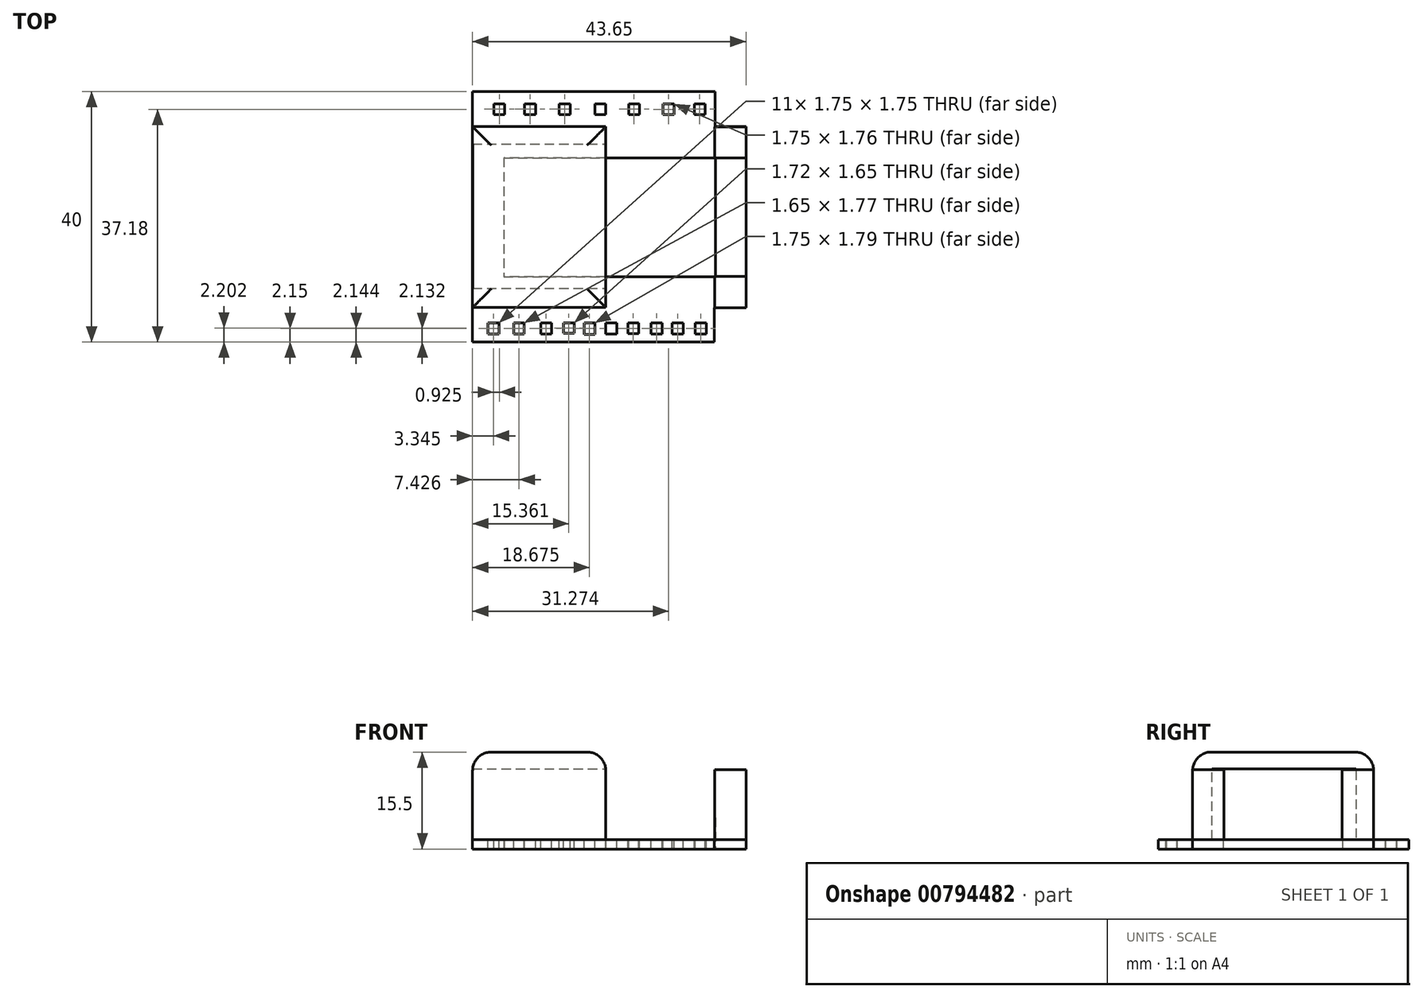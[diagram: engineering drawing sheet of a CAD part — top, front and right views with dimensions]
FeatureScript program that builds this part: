
annotation { "Feature Type Name" : "Feature", "Feature Type Description" : "" }
export const myFeature = defineFeature(function(context is Context, id is Id, definition is map)
    precondition{}
    {
        {
            var Q0;
            Q0=qCreatedBy(makeId("Top.planeOp"),FACE);
            var sketch = newSketch(context, id + "F0", { "sketchPlane" : qUnion([Q0])});
            skLineSegment(sketch, "E0.bottom", {"start": v(-21.27, 7.67) * mm, "end": v(22.37, 7.67) * mm});
            skLineSegment(sketch, "E0.top", {"start": v(-21.27, -21.23) * mm, "end": v(22.37, -21.23) * mm});
            skLineSegment(sketch, "E0.left", {"start": v(-21.27, 7.67) * mm, "end": v(-21.27, -21.23) * mm});
            skLineSegment(sketch, "E0.right", {"start": v(22.37, 7.67) * mm, "end": v(22.37, -21.23) * mm});
            skLineSegment(sketch, "E1.bottom", {"start": v(22.37, 7.67) * mm, "end": v(0, 7.67) * mm});
            skLineSegment(sketch, "E1.top", {"start": v(22.37, -21.23) * mm, "end": v(0, -21.23) * mm});
            skLineSegment(sketch, "E2.bottom", {"start": v(-21.27, 7.67) * mm, "end": v(-16.27, 7.67) * mm});
            skLineSegment(sketch, "E2.top", {"start": v(-21.27, 2.67) * mm, "end": v(-16.27, 2.67) * mm});
            skLineSegment(sketch, "E2.left", {"start": v(-21.27, 7.67) * mm, "end": v(-21.27, 2.67) * mm});
            skLineSegment(sketch, "E2.right", {"start": v(-16.27, 7.67) * mm, "end": v(-16.27, 2.67) * mm});
            skLineSegment(sketch, "E3.bottom", {"start": v(-21.27, -21.23) * mm, "end": v(-16.27, -21.23) * mm});
            skLineSegment(sketch, "E3.top", {"start": v(-21.27, -16.23) * mm, "end": v(-16.27, -16.23) * mm});
            skLineSegment(sketch, "E3.left", {"start": v(-21.27, -21.23) * mm, "end": v(-21.27, -16.23) * mm});
            skLineSegment(sketch, "E3.right", {"start": v(-16.27, -21.23) * mm, "end": v(-16.27, -16.23) * mm});
            skLineSegment(sketch, "E4.bottom", {"start": v(22.37, -21.23) * mm, "end": v(17.37, -21.23) * mm});
            skLineSegment(sketch, "E4.top", {"start": v(22.37, -16.23) * mm, "end": v(17.37, -16.23) * mm});
            skLineSegment(sketch, "E4.left", {"start": v(22.37, -21.23) * mm, "end": v(22.37, -16.23) * mm});
            skLineSegment(sketch, "E4.right", {"start": v(17.37, -21.23) * mm, "end": v(17.37, -16.23) * mm});
            skLineSegment(sketch, "E5.bottom", {"start": v(22.37, 7.67) * mm, "end": v(17.37, 7.67) * mm});
            skLineSegment(sketch, "E5.top", {"start": v(22.37, 2.67) * mm, "end": v(17.37, 2.67) * mm});
            skLineSegment(sketch, "E5.left", {"start": v(22.37, 7.67) * mm, "end": v(22.37, 2.67) * mm});
            skLineSegment(sketch, "E5.right", {"start": v(17.37, 7.67) * mm, "end": v(17.37, 2.67) * mm});
            skSolve(sketch);
        }
        {
            var Q0;
            Q0 = qSketchRegion(id + "F0", true);
            extrude(context, id + "F1", {"entities" : qUnion([Q0]), "oppositeDirection" : true, "depth" : 1.5 * mm, "offsetDistance" : 25 * mm});
        }
        {
            var Q0;
            Q0=makeQuery(id+"F0.imprint","IMPRINT",FACE,{"disambiguationData":[TD([[makeQuery(id+"F0.imprint","IMPRINT",EDGE,{"derivedFrom":sQuery(id+"F0.wireOp",EDGE,"E0.bottom")}),-1.0]])]});
            var sketch = newSketch(context, id + "F2", { "sketchPlane" : qUnion([Q0])});
            skLineSegment(sketch, "E6.bottom", {"start": v(17.38, 7.65) * mm, "end": v(22.38, 7.65) * mm});
            skLineSegment(sketch, "E6.top", {"start": v(17.38, 2.65) * mm, "end": v(22.38, 2.65) * mm});
            skLineSegment(sketch, "E6.left", {"start": v(17.38, 7.65) * mm, "end": v(17.38, 2.65) * mm});
            skLineSegment(sketch, "E6.right", {"start": v(22.38, 7.65) * mm, "end": v(22.38, 2.65) * mm});
            skLineSegment(sketch, "E7.bottom", {"start": v(22.38, -21.25) * mm, "end": v(17.38, -21.25) * mm});
            skLineSegment(sketch, "E7.top", {"start": v(22.38, -16.25) * mm, "end": v(17.38, -16.25) * mm});
            skLineSegment(sketch, "E7.left", {"start": v(22.38, -21.25) * mm, "end": v(22.38, -16.25) * mm});
            skLineSegment(sketch, "E7.right", {"start": v(17.38, -21.25) * mm, "end": v(17.38, -16.25) * mm});
            skSolve(sketch);
        }
        {
            var Q0;
            Q0 = qSketchRegion(id + "F2", true);
            extrude(context, id + "F3", {"entities" : qUnion([Q0]), "operationType" : NewBodyOperationType.ADD, "depth" : 11.2 * mm, "offsetDistance" : 25 * mm});
        }
        {
            var Q0;
            Q0=makeQuery(id+"F0.imprint","IMPRINT",FACE,{"disambiguationData":[TD([[makeQuery(id+"F0.imprint","IMPRINT",EDGE,{"derivedFrom":sQuery(id+"F0.wireOp",EDGE,"E0.bottom")}),-1.0]])]});
            var sketch = newSketch(context, id + "F4", { "sketchPlane" : qUnion([Q0])});
            skLineSegment(sketch, "E8.bottom", {"start": v(-21.27, 7.67) * mm, "end": v(0, 7.67) * mm});
            skLineSegment(sketch, "E8.top", {"start": v(-21.27, -21.23) * mm, "end": v(0, -21.23) * mm});
            skLineSegment(sketch, "E8.left", {"start": v(-21.27, 7.67) * mm, "end": v(-21.27, -21.23) * mm});
            skLineSegment(sketch, "E8.right", {"start": v(0, 7.67) * mm, "end": v(0, -21.23) * mm});
            skSolve(sketch);
        }
        {
            var Q0;
            Q0 = qSketchRegion(id + "F4", true);
            extrude(context, id + "F5", {"entities" : qUnion([Q0]), "operationType" : NewBodyOperationType.ADD, "depth" : 14 * mm, "offsetDistance" : 25 * mm});
        }
        {
            var Q0;
            Q0=makeQuery(id+"F5.opExtrude","SWEPT_FACE",FACE,{"disambiguationData":[OSD([sQuery(id+"F4.wireOp",EDGE,"E8.right")])]});
            var sketch = newSketch(context, id + "F6", { "sketchPlane" : qUnion([Q0])});
            skLineSegment(sketch, "E9.bottom", {"start": v(-18.14, 11.3) * mm, "end": v(4.86, 11.3) * mm});
            skLineSegment(sketch, "E9.top", {"start": v(-18.14, 0) * mm, "end": v(4.86, 0) * mm});
            skLineSegment(sketch, "E9.left", {"start": v(-18.14, 11.3) * mm, "end": v(-18.14, 0) * mm});
            skLineSegment(sketch, "E9.right", {"start": v(4.86, 11.3) * mm, "end": v(4.86, 0) * mm});
            skLineSegment(sketch, "E10", {"start": v(4.86, 11.3) * mm, "end": v(7.67, 11.3) * mm});
            skSolve(sketch);
        }
        {
            var Q0;
            Q0 = qSketchRegion(id + "F6", true);
            extrude(context, id + "F7", {"entities" : qUnion([Q0]), "operationType" : NewBodyOperationType.REMOVE, "oppositeDirection" : true, "depth" : 37.2 * mm, "offsetDistance" : 25 * mm});
        }
        {
            var Q0;
            Q0=makeQuery(id+"F1.opExtrude","SWEPT_FACE",FACE,{"disambiguationData":[OSD([sQuery(id+"F0.wireOp",EDGE,"E0.top"),sQuery(id+"F0.wireOp",EDGE,"E1.top"),sQuery(id+"F0.wireOp",EDGE,"E3.bottom"),sQuery(id+"F0.wireOp",EDGE,"E4.bottom")])]});
            var sketch = newSketch(context, id + "F8", { "sketchPlane" : qUnion([Q0])});
            skLineSegment(sketch, "E11.bottom", {"start": v(-21.27, 0) * mm, "end": v(22.37, 0) * mm});
            skLineSegment(sketch, "E11.top", {"start": v(-21.27, -1.5) * mm, "end": v(22.37, -1.5) * mm});
            skLineSegment(sketch, "E11.left", {"start": v(-21.27, 0) * mm, "end": v(-21.27, -1.5) * mm});
            skLineSegment(sketch, "E11.right", {"start": v(22.37, 0) * mm, "end": v(22.37, -1.5) * mm});
            skSolve(sketch);
        }
        {
            var Q0;
            Q0 = qSketchRegion(id + "F8", true);
            extrude(context, id + "F9", {"entities" : qUnion([Q0]), "operationType" : NewBodyOperationType.ADD, "depth" : 10 * mm, "offsetDistance" : 25 * mm});
        }
        {
            var Q0;
            Q0=makeQuery(id+"F1.opExtrude","SWEPT_FACE",FACE,{"disambiguationData":[OSD([sQuery(id+"F0.wireOp",EDGE,"E0.bottom"),sQuery(id+"F0.wireOp",EDGE,"E1.bottom"),sQuery(id+"F0.wireOp",EDGE,"E2.bottom"),sQuery(id+"F0.wireOp",EDGE,"E5.bottom")])]});
            var sketch = newSketch(context, id + "F10", { "sketchPlane" : qUnion([Q0])});
            skLineSegment(sketch, "E12.bottom", {"start": v(-22.37, 0) * mm, "end": v(21.27, 0) * mm});
            skLineSegment(sketch, "E12.top", {"start": v(-22.37, -1.5) * mm, "end": v(21.27, -1.5) * mm});
            skLineSegment(sketch, "E12.left", {"start": v(-22.37, 0) * mm, "end": v(-22.37, -1.5) * mm});
            skLineSegment(sketch, "E12.right", {"start": v(21.27, 0) * mm, "end": v(21.27, -1.5) * mm});
            skSolve(sketch);
        }
        {
            var Q0;
            Q0 = qSketchRegion(id + "F10", true);
            extrude(context, id + "F11", {"entities" : qUnion([Q0]), "operationType" : NewBodyOperationType.ADD, "depth" : 10 * mm, "offsetDistance" : 25 * mm});
        }
        {
            var Q0;
            Q0=qCreatedBy(makeId("Top.planeOp"),FACE);
            var sketch = newSketch(context, id + "F12", { "sketchPlane" : qUnion([Q0])});
            skLineSegment(sketch, "E13.bottom", {"start": v(-18.8, -25.45) * mm, "end": v(-17.05, -25.45) * mm});
            skLineSegment(sketch, "E13.top", {"start": v(-18.8, -23.7) * mm, "end": v(-17.05, -23.7) * mm});
            skLineSegment(sketch, "E13.left", {"start": v(-18.8, -25.45) * mm, "end": v(-18.8, -23.7) * mm});
            skLineSegment(sketch, "E13.right", {"start": v(-17.05, -25.45) * mm, "end": v(-17.05, -23.7) * mm});
            skLineSegment(sketch, "E14.bottom", {"start": v(-10.4, -25.45) * mm, "end": v(-8.64, -25.45) * mm});
            skLineSegment(sketch, "E14.top", {"start": v(-10.4, -23.7) * mm, "end": v(-8.64, -23.7) * mm});
            skLineSegment(sketch, "E14.left", {"start": v(-10.4, -25.45) * mm, "end": v(-10.4, -23.7) * mm});
            skLineSegment(sketch, "E14.right", {"start": v(-8.64, -25.45) * mm, "end": v(-8.64, -23.7) * mm});
            skLineSegment(sketch, "E15.bottom", {"start": v(0, -25.45) * mm, "end": v(1.75, -25.45) * mm});
            skLineSegment(sketch, "E15.top", {"start": v(0, -23.7) * mm, "end": v(1.75, -23.7) * mm});
            skLineSegment(sketch, "E15.left", {"start": v(0, -25.45) * mm, "end": v(0, -23.7) * mm});
            skLineSegment(sketch, "E15.right", {"start": v(1.75, -25.45) * mm, "end": v(1.75, -23.7) * mm});
            skLineSegment(sketch, "E16.bottom", {"start": v(10.6, -25.45) * mm, "end": v(12.35, -25.45) * mm});
            skLineSegment(sketch, "E16.top", {"start": v(10.6, -23.7) * mm, "end": v(12.35, -23.7) * mm});
            skLineSegment(sketch, "E16.left", {"start": v(10.6, -25.45) * mm, "end": v(10.6, -23.7) * mm});
            skLineSegment(sketch, "E16.right", {"start": v(12.35, -25.45) * mm, "end": v(12.35, -23.7) * mm});
            skLineSegment(sketch, "E17.bottom", {"start": v(-14.67, -23.7) * mm, "end": v(-13.02, -23.7) * mm});
            skLineSegment(sketch, "E17.top", {"start": v(-14.67, -25.47) * mm, "end": v(-13.02, -25.47) * mm});
            skLineSegment(sketch, "E17.left", {"start": v(-14.67, -23.7) * mm, "end": v(-14.67, -25.47) * mm});
            skLineSegment(sketch, "E17.right", {"start": v(-13.02, -23.7) * mm, "end": v(-13.02, -25.47) * mm});
            skLineSegment(sketch, "E18.bottom", {"start": v(-6.77, -23.7) * mm, "end": v(-5.05, -23.7) * mm});
            skLineSegment(sketch, "E18.top", {"start": v(-6.77, -25.35) * mm, "end": v(-5.05, -25.35) * mm});
            skLineSegment(sketch, "E18.left", {"start": v(-6.77, -23.7) * mm, "end": v(-6.77, -25.35) * mm});
            skLineSegment(sketch, "E18.right", {"start": v(-5.05, -23.7) * mm, "end": v(-5.05, -25.35) * mm});
            skLineSegment(sketch, "E19.bottom", {"start": v(-3.47, -23.7) * mm, "end": v(-1.72, -23.7) * mm});
            skLineSegment(sketch, "E19.top", {"start": v(-3.47, -25.5) * mm, "end": v(-1.72, -25.5) * mm});
            skLineSegment(sketch, "E19.left", {"start": v(-3.47, -23.7) * mm, "end": v(-3.47, -25.5) * mm});
            skLineSegment(sketch, "E19.right", {"start": v(-1.72, -23.7) * mm, "end": v(-1.72, -25.5) * mm});
            skLineSegment(sketch, "E20.bottom", {"start": v(3.5, -23.67) * mm, "end": v(5.25, -23.67) * mm});
            skLineSegment(sketch, "E20.top", {"start": v(3.5, -25.42) * mm, "end": v(5.25, -25.42) * mm});
            skLineSegment(sketch, "E20.left", {"start": v(3.5, -23.67) * mm, "end": v(3.5, -25.42) * mm});
            skLineSegment(sketch, "E20.right", {"start": v(5.25, -23.67) * mm, "end": v(5.25, -25.42) * mm});
            skLineSegment(sketch, "E21.bottom", {"start": v(7.25, -23.69) * mm, "end": v(9, -23.69) * mm});
            skLineSegment(sketch, "E21.top", {"start": v(7.25, -25.44) * mm, "end": v(9, -25.44) * mm});
            skLineSegment(sketch, "E21.left", {"start": v(7.25, -23.69) * mm, "end": v(7.25, -25.44) * mm});
            skLineSegment(sketch, "E21.right", {"start": v(9, -23.69) * mm, "end": v(9, -25.44) * mm});
            skLineSegment(sketch, "E22.bottom", {"start": v(14.27, -23.7) * mm, "end": v(16.02, -23.7) * mm});
            skLineSegment(sketch, "E22.top", {"start": v(14.27, -25.45) * mm, "end": v(16.02, -25.45) * mm});
            skLineSegment(sketch, "E22.left", {"start": v(14.27, -23.7) * mm, "end": v(14.27, -25.45) * mm});
            skLineSegment(sketch, "E22.right", {"start": v(16.02, -23.7) * mm, "end": v(16.02, -25.45) * mm});
            skLineSegment(sketch, "E23.bottom", {"start": v(-21.26, -26.73) * mm, "end": v(17.3, -26.73) * mm});
            skLineSegment(sketch, "E23.top", {"start": v(-21.26, -33.32) * mm, "end": v(17.3, -33.32) * mm});
            skLineSegment(sketch, "E23.left", {"start": v(-21.26, -26.73) * mm, "end": v(-21.26, -33.32) * mm});
            skLineSegment(sketch, "E23.right", {"start": v(17.3, -26.73) * mm, "end": v(17.3, -33.32) * mm});
            skLineSegment(sketch, "E24.bottom", {"start": v(17.3, -21.26) * mm, "end": v(23.15, -21.26) * mm});
            skLineSegment(sketch, "E24.top", {"start": v(17.3, -33.32) * mm, "end": v(23.15, -33.32) * mm});
            skLineSegment(sketch, "E24.left", {"start": v(17.3, -21.26) * mm, "end": v(17.3, -33.32) * mm});
            skLineSegment(sketch, "E24.right", {"start": v(23.15, -21.26) * mm, "end": v(23.15, -33.32) * mm});
            skSolve(sketch);
        }
        {
            var Q0;
            Q0 = qSketchRegion(id + "F12", true);
            extrude(context, id + "F13", {"entities" : qUnion([Q0]), "operationType" : NewBodyOperationType.REMOVE, "oppositeDirection" : true, "depth" : 25 * mm, "offsetDistance" : 25 * mm});
        }
        {
            var Q0;
            Q0=makeQuery(id+"F11.opExtrude","SWEPT_FACE",FACE,{"disambiguationData":[OSD([sQuery(id+"F10.wireOp",EDGE,"E12.bottom")])]});
            var sketch = newSketch(context, id + "F14", { "sketchPlane" : qUnion([Q0])});
            skLineSegment(sketch, "E25.bottom", {"start": v(-17.87, 11.33) * mm, "end": v(-16.12, 11.33) * mm});
            skLineSegment(sketch, "E25.top", {"start": v(-17.87, 9.58) * mm, "end": v(-16.12, 9.58) * mm});
            skLineSegment(sketch, "E25.left", {"start": v(-17.87, 11.33) * mm, "end": v(-17.87, 9.58) * mm});
            skLineSegment(sketch, "E25.right", {"start": v(-16.12, 11.33) * mm, "end": v(-16.12, 9.58) * mm});
            skLineSegment(sketch, "E26.bottom", {"start": v(-7.45, 11.33) * mm, "end": v(-5.7, 11.33) * mm});
            skLineSegment(sketch, "E26.top", {"start": v(-7.45, 9.58) * mm, "end": v(-5.7, 9.58) * mm});
            skLineSegment(sketch, "E26.left", {"start": v(-7.45, 11.33) * mm, "end": v(-7.45, 9.58) * mm});
            skLineSegment(sketch, "E26.right", {"start": v(-5.7, 11.33) * mm, "end": v(-5.7, 9.58) * mm});
            skLineSegment(sketch, "E27.bottom", {"start": v(3.64, 11.33) * mm, "end": v(5.39, 11.33) * mm});
            skLineSegment(sketch, "E27.top", {"start": v(3.64, 9.58) * mm, "end": v(5.39, 9.58) * mm});
            skLineSegment(sketch, "E27.left", {"start": v(3.64, 11.33) * mm, "end": v(3.64, 9.58) * mm});
            skLineSegment(sketch, "E27.right", {"start": v(5.39, 11.33) * mm, "end": v(5.39, 9.58) * mm});
            skLineSegment(sketch, "E28.bottom", {"start": v(14.12, 11.33) * mm, "end": v(15.87, 11.33) * mm});
            skLineSegment(sketch, "E28.top", {"start": v(14.12, 9.58) * mm, "end": v(15.87, 9.58) * mm});
            skLineSegment(sketch, "E28.left", {"start": v(14.12, 11.33) * mm, "end": v(14.12, 9.58) * mm});
            skLineSegment(sketch, "E28.right", {"start": v(15.87, 11.33) * mm, "end": v(15.87, 9.58) * mm});
            skLineSegment(sketch, "E29.bottom", {"start": v(9.13, 11.33) * mm, "end": v(10.88, 11.33) * mm});
            skLineSegment(sketch, "E29.top", {"start": v(9.13, 9.57) * mm, "end": v(10.88, 9.57) * mm});
            skLineSegment(sketch, "E29.left", {"start": v(9.13, 11.33) * mm, "end": v(9.13, 9.57) * mm});
            skLineSegment(sketch, "E29.right", {"start": v(10.88, 11.33) * mm, "end": v(10.88, 9.57) * mm});
            skLineSegment(sketch, "E30.bottom", {"start": v(0, 9.57) * mm, "end": v(-1.75, 9.57) * mm});
            skLineSegment(sketch, "E30.top", {"start": v(0, 11.32) * mm, "end": v(-1.75, 11.32) * mm});
            skLineSegment(sketch, "E30.left", {"start": v(0, 9.57) * mm, "end": v(0, 11.32) * mm});
            skLineSegment(sketch, "E30.right", {"start": v(-1.75, 9.57) * mm, "end": v(-1.75, 11.32) * mm});
            skLineSegment(sketch, "E31.bottom", {"start": v(-11.22, 9.58) * mm, "end": v(-12.97, 9.58) * mm});
            skLineSegment(sketch, "E31.top", {"start": v(-11.22, 11.33) * mm, "end": v(-12.97, 11.33) * mm});
            skLineSegment(sketch, "E31.left", {"start": v(-11.22, 9.58) * mm, "end": v(-11.22, 11.33) * mm});
            skLineSegment(sketch, "E31.right", {"start": v(-12.97, 9.58) * mm, "end": v(-12.97, 11.33) * mm});
            skLineSegment(sketch, "E32.bottom", {"start": v(-22.4, 13.27) * mm, "end": v(28.41, 13.27) * mm});
            skLineSegment(sketch, "E32.top", {"start": v(-22.4, 19.1) * mm, "end": v(28.41, 19.1) * mm});
            skLineSegment(sketch, "E32.left", {"start": v(-22.4, 13.27) * mm, "end": v(-22.4, 19.1) * mm});
            skLineSegment(sketch, "E32.right", {"start": v(28.41, 13.27) * mm, "end": v(28.41, 19.1) * mm});
            skLineSegment(sketch, "E33.bottom", {"start": v(28.12, 7.67) * mm, "end": v(17.44, 7.67) * mm});
            skLineSegment(sketch, "E33.top", {"start": v(28.12, 21.33) * mm, "end": v(17.44, 21.33) * mm});
            skLineSegment(sketch, "E33.left", {"start": v(28.12, 7.67) * mm, "end": v(28.12, 21.33) * mm});
            skLineSegment(sketch, "E33.right", {"start": v(17.44, 7.67) * mm, "end": v(17.44, 21.33) * mm});
            skSolve(sketch);
        }
        {
            var Q0;
            Q0 = qSketchRegion(id + "F14", true);
            extrude(context, id + "F15", {"entities" : qUnion([Q0]), "operationType" : NewBodyOperationType.REMOVE, "oppositeDirection" : true, "depth" : 25 * mm, "offsetDistance" : 25 * mm});
        }
        {
            var Q0;
            Q0=makeQuery(id+"F1.opExtrude","CAP_FACE",FACE,{"disambiguationData":[OSD([sQuery(id+"F0.wireOp",EDGE,"E0.bottom"),sQuery(id+"F0.wireOp",EDGE,"E0.top"),sQuery(id+"F0.wireOp",EDGE,"E0.left"),sQuery(id+"F0.wireOp",EDGE,"E1.bottom"),sQuery(id+"F0.wireOp",EDGE,"E1.top"),sQuery(id+"F0.wireOp",EDGE,"E0.right"),sQuery(id+"F0.wireOp",EDGE,"E2.bottom"),sQuery(id+"F0.wireOp",EDGE,"E2.left"),sQuery(id+"F0.wireOp",EDGE,"E3.bottom"),sQuery(id+"F0.wireOp",EDGE,"E3.left"),sQuery(id+"F0.wireOp",EDGE,"E4.bottom"),sQuery(id+"F0.wireOp",EDGE,"E4.left"),sQuery(id+"F0.wireOp",EDGE,"E5.bottom"),sQuery(id+"F0.wireOp",EDGE,"E5.left")])],"isStart":false});
            var sketch = newSketch(context, id + "F16", { "sketchPlane" : qUnion([Q0])});
            skLineSegment(sketch, "E34.bottom", {"start": v(-16.3, 16.34) * mm, "end": v(17.48, 16.34) * mm});
            skLineSegment(sketch, "E34.top", {"start": v(-16.3, -2.7) * mm, "end": v(17.48, -2.7) * mm});
            skLineSegment(sketch, "E34.left", {"start": v(-16.3, 16.34) * mm, "end": v(-16.3, -2.7) * mm});
            skLineSegment(sketch, "E34.right", {"start": v(17.48, 16.34) * mm, "end": v(17.48, -2.7) * mm});
            skSolve(sketch);
        }
        {
            var Q0;
            Q0=makeQuery(id+"F16.imprint","IMPRINT",FACE,{"disambiguationData":[TD([[makeQuery(id+"F16.imprint","IMPRINT",EDGE,{"derivedFrom":sQuery(id+"F16.wireOp",EDGE,"E34.bottom")}),-1.0]])]});
            extrude(context, id + "F17", {"entities" : qUnion([Q0]), "operationType" : NewBodyOperationType.REMOVE, "oppositeDirection" : true, "depth" : 5 * mm, "offsetDistance" : 25 * mm});
        }
        {
            var Q0;
            Q0=makeQuery(id+"F5.opExtrude","CAP_FACE",FACE,{"disambiguationData":[OSD([sQuery(id+"F4.wireOp",EDGE,"E8.bottom"),sQuery(id+"F4.wireOp",EDGE,"E8.top"),sQuery(id+"F4.wireOp",EDGE,"E8.left"),sQuery(id+"F4.wireOp",EDGE,"E8.right")])],"isStart":false});
            fillet(context, id + "F18", {"entities" : qUnion([Q0]), "radius" : 3 * mm, "tangentPropagation" : true, "allowEdgeOverflow" : false});
        }
    });
